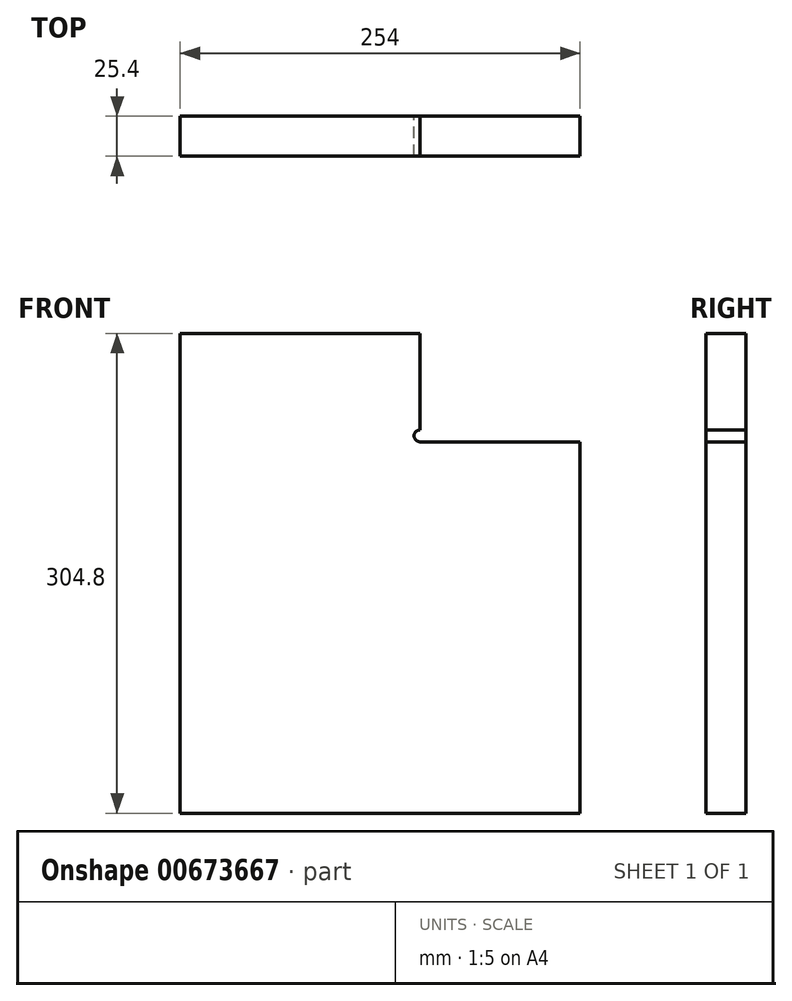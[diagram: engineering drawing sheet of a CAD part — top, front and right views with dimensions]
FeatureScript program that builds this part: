
annotation { "Feature Type Name" : "Feature", "Feature Type Description" : "" }
export const myFeature = defineFeature(function(context is Context, id is Id, definition is map)
    precondition{}
    {
        {
            var Q0;
            Q0=qCreatedBy(makeId("Front.planeOp"),FACE);
            var sketch = newSketch(context, id + "F0", { "sketchPlane" : qUnion([Q0])});
            skLineSegment(sketch, "E0.bottom", {"start": v(-166.35, -118.53) * mm, "end": v(87.65, -118.53) * mm});
            skLineSegment(sketch, "E0.top", {"start": v(-166.35, 186.27) * mm, "end": v(-13.95, 186.27) * mm});
            skLineSegment(sketch, "E0.left", {"start": v(-166.35, -118.53) * mm, "end": v(-166.35, 186.27) * mm});
            skLineSegment(sketch, "E0.right", {"start": v(87.65, -118.53) * mm, "end": v(87.65, 117.38) * mm});
            skLineSegment(sketch, "E1.top", {"start": v(87.65, 117.38) * mm, "end": v(-13.95, 117.38) * mm});
            skLineSegment(sketch, "E1.right", {"start": v(-13.95, 186.27) * mm, "end": v(-13.95, 125) * mm});
            skArc(sketch, "E2", {"start": v(-13.95, 117.38) * mm, "mid": v(-17.76, 121.2) * mm, "end": v(-13.95, 125) * mm});
            skSolve(sketch);
        }
        {
            var Q0;
            Q0=makeQuery(id+"F0.imprint","IMPRINT",FACE,{"disambiguationData":[TD([[makeQuery(id+"F0.imprint","IMPRINT",EDGE,{"derivedFrom":sQuery(id+"F0.wireOp",EDGE,"E0.bottom")}),1.0]])]});
            extrude(context, id + "F1", {"entities" : qUnion([Q0]), "endBound" : BoundingType.SYMMETRIC, "depth" : 25.4 * mm, "offsetDistance" : 25.4 * mm});
        }
    });
